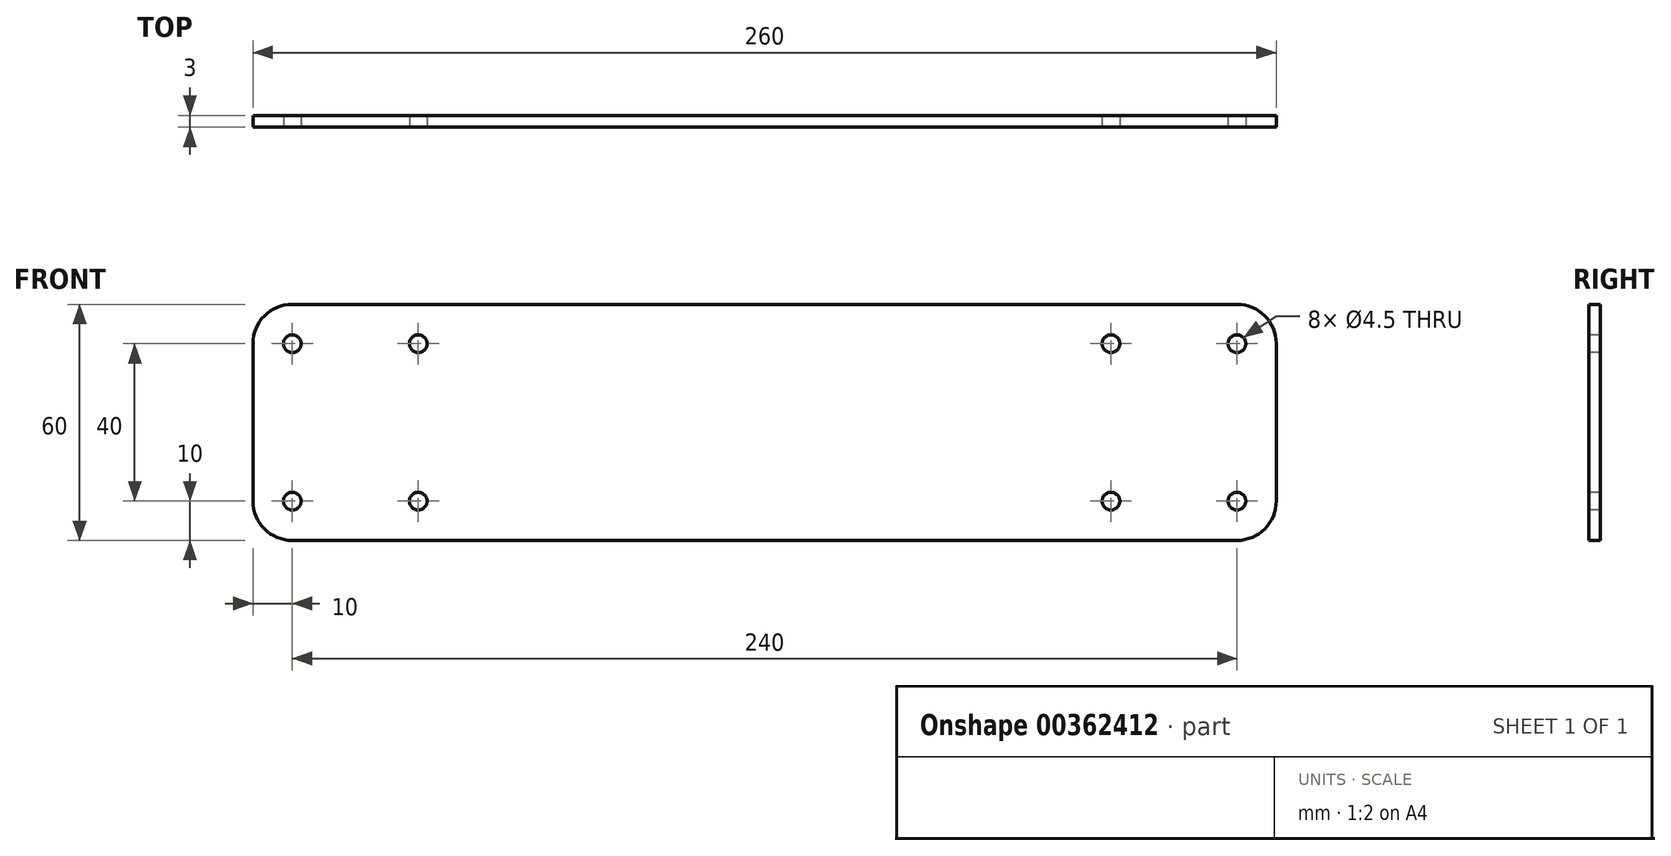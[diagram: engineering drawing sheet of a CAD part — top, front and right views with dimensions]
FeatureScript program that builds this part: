
annotation { "Feature Type Name" : "Feature", "Feature Type Description" : "" }
export const myFeature = defineFeature(function(context is Context, id is Id, definition is map)
    precondition{}
    {
        {
            var Q0;
            Q0=qCreatedBy(makeId("Front.planeOp"),FACE);
            var sketch = newSketch(context, id + "F0", { "sketchPlane" : qUnion([Q0])});
            skLineSegment(sketch, "E0.bottom", {"start": v(130, -30) * mm, "end": v(-130, -30) * mm});
            skLineSegment(sketch, "E0.top", {"start": v(130, 30) * mm, "end": v(-130, 30) * mm});
            skLineSegment(sketch, "E0.left", {"start": v(130, -30) * mm, "end": v(130, 30) * mm});
            skLineSegment(sketch, "E0.right", {"start": v(-130, -30) * mm, "end": v(-130, 30) * mm});
            skPoint(sketch, "E0.middle", {"position": v(0, 0) * mm});
            skSolve(sketch);
        }
        {
            var Q0;
            Q0=qSketchRegion(id+"F0",true);
            extrude(context, id + "F1", {"entities" : qUnion([Q0]), "depth" : 3 * mm});
        }
        {
            var Q0;
            Q0=makeQuery(id+"F1.opExtrude","CAP_FACE",FACE,{"disambiguationData":[OSD([sQuery(id+"F0.wireOp",EDGE,"E0.bottom"),sQuery(id+"F0.wireOp",EDGE,"E0.top"),sQuery(id+"F0.wireOp",EDGE,"E0.left"),sQuery(id+"F0.wireOp",EDGE,"E0.right")])],"isStart":false});
            var sketch = newSketch(context, id + "F2", { "sketchPlane" : qUnion([Q0])});
            skCircle(sketch, "E1", {"center": v(-120, 20) * mm, "radius": 2.25 * mm});
            skCircle(sketch, "E2.0.1.0", {"center": v(-120, -20) * mm, "radius": 2.25 * mm});
            skCircle(sketch, "E2.1.0.0", {"center": v(-88, 20) * mm, "radius": 2.25 * mm});
            skCircle(sketch, "E2.1.1.0", {"center": v(-88, -20) * mm, "radius": 2.25 * mm});
            skLineSegment(sketch, "E2.direction1", {"start": v(-120, 20) * mm, "end": v(-88, 20) * mm, "construction": true});
            skLineSegment(sketch, "E2.direction2", {"start": v(-120, 20) * mm, "end": v(-120, -20) * mm, "construction": true});
            skLineSegment(sketch, "E3", {"start": v(0, 30) * mm, "end": v(0, -30) * mm});
            skCircle(sketch, "E4.MirrorC", {"center": v(88, 20) * mm, "radius": 2.25 * mm});
            skCircle(sketch, "E5.MirrorC", {"center": v(120, 20) * mm, "radius": 2.25 * mm});
            skCircle(sketch, "E6.MirrorC", {"center": v(120, -20) * mm, "radius": 2.25 * mm});
            skCircle(sketch, "E7.MirrorC", {"center": v(88, -20) * mm, "radius": 2.25 * mm});
            skSolve(sketch);
        }
        {
            var Q0;
            Q0=qSketchRegion(id+"F2",true);
            extrude(context, id + "F3", {"entities" : qUnion([Q0]), "operationType" : NewBodyOperationType.REMOVE, "endBound" : BoundingType.THROUGH_ALL, "oppositeDirection" : true, "depth" : 25 * mm});
        }
        {
            var Q0;
            Q0=makeQuery(id+"F1.opExtrude","SWEPT_EDGE",EDGE,{"disambiguationData":[OSD([sQuery(id+"F0.wireOp",EDGE,"E0.top"),sQuery(id+"F0.wireOp",EDGE,"E0.right")])]});
            var Q1;
            Q1=makeQuery(id+"F1.opExtrude","SWEPT_EDGE",EDGE,{"disambiguationData":[OSD([sQuery(id+"F0.wireOp",EDGE,"E0.bottom"),sQuery(id+"F0.wireOp",EDGE,"E0.right")])]});
            var Q2;
            Q2=makeQuery(id+"F1.opExtrude","SWEPT_EDGE",EDGE,{"disambiguationData":[OSD([sQuery(id+"F0.wireOp",EDGE,"E0.bottom"),sQuery(id+"F0.wireOp",EDGE,"E0.left")])]});
            var Q3;
            Q3=makeQuery(id+"F1.opExtrude","SWEPT_EDGE",EDGE,{"disambiguationData":[OSD([sQuery(id+"F0.wireOp",EDGE,"E0.top"),sQuery(id+"F0.wireOp",EDGE,"E0.left")])]});
            fillet(context, id + "F4", {"entities" : qUnion([Q0, Q1, Q2, Q3]), "radius" : 10 * mm, "tangentPropagation" : true, "allowEdgeOverflow" : false});
        }
    });
